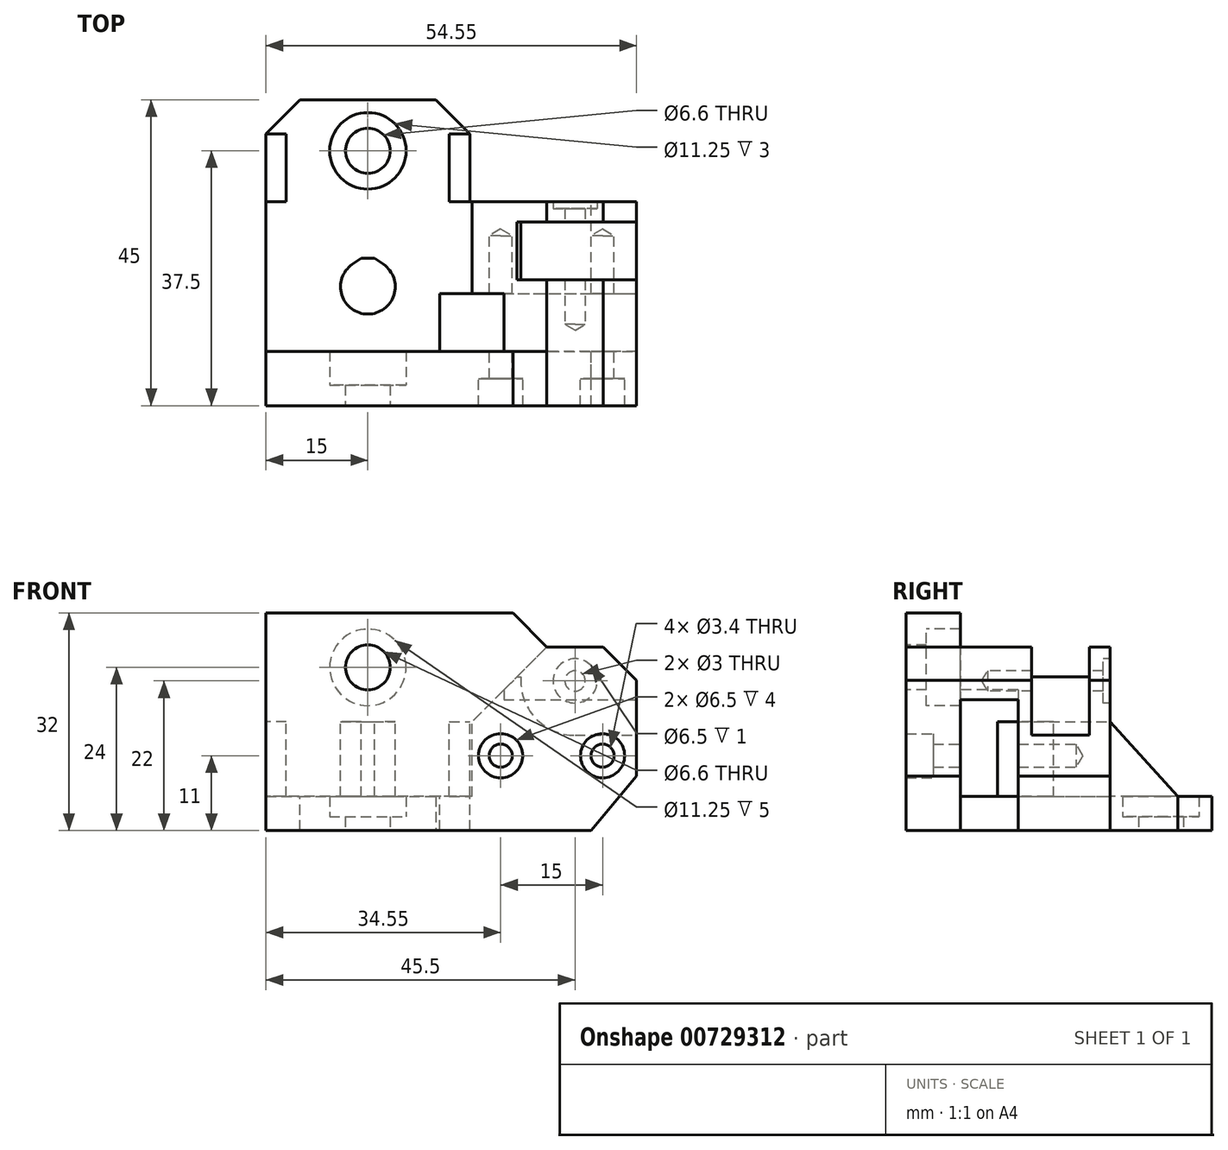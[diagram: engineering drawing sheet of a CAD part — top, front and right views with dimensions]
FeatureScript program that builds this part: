
annotation { "Feature Type Name" : "Feature", "Feature Type Description" : "" }
export const myFeature = defineFeature(function(context is Context, id is Id, definition is map)
    precondition{}
    {
        {
            var Q0;
            Q0=qCreatedBy(makeId("Front.planeOp"),FACE);
            var sketch = newSketch(context, id + "F0", { "sketchPlane" : qUnion([Q0])});
            skLineSegment(sketch, "E0", {"start": v(19.55, 11) * mm, "end": v(34.55, 11) * mm, "construction": true});
            skLineSegment(sketch, "E1", {"start": v(34.55, 11) * mm, "end": v(30.5, 22) * mm, "construction": true});
            skLineSegment(sketch, "E2", {"start": v(30.5, 22) * mm, "end": v(19.55, 11) * mm, "construction": true});
            skPoint(sketch, "E3", {"position": v(30.5, 22) * mm});
            skPoint(sketch, "E4", {"position": v(34.55, 11) * mm});
            skPoint(sketch, "E5", {"position": v(19.55, 11) * mm});
            skCircle(sketch, "E6", {"center": v(30.5, 22) * mm, "radius": 1.5 * mm, "construction": true});
            skCircle(sketch, "E7", {"center": v(34.55, 11) * mm, "radius": 1.5 * mm, "construction": true});
            skCircle(sketch, "E8", {"center": v(19.55, 11) * mm, "radius": 1.5 * mm, "construction": true});
            skPoint(sketch, "E9", {"position": v(0, 0) * mm});
            skCircle(sketch, "E10", {"center": v(30.5, 22) * mm, "radius": 6.5 * mm, "construction": true});
            skCircle(sketch, "E11", {"center": v(34.55, 11) * mm, "radius": 6.5 * mm, "construction": true});
            skCircle(sketch, "E12", {"center": v(19.55, 11) * mm, "radius": 6.5 * mm, "construction": true});
            skPoint(sketch, "E13", {"position": v(34.55, 12.5) * mm});
            skPoint(sketch, "E14", {"position": v(30.5, 15.5) * mm});
            skSolve(sketch);
        }
        {
            var Q0;
            Q0=qCreatedBy(makeId("Front.planeOp"),FACE);
            cPlane(context, id + "F1", {"entities" : qUnion([Q0]), "cplaneType" : CPlaneType.OFFSET, "offset" : 12.5 * mm, "oppositeDirection" : true, "width" : 150 * mm, "height" : 150 * mm});
        }
        {
            var Q0;
            Q0=qCreatedBy(id+"F1.planeOp",FACE);
            cPlane(context, id + "F2", {"entities" : qUnion([Q0]), "cplaneType" : CPlaneType.OFFSET, "offset" : 30 * mm, "width" : 150 * mm, "height" : 150 * mm});
        }
        {
            var Q0;
            Q0=qCreatedBy(id+"F1.planeOp",FACE);
            var sketch = newSketch(context, id + "F3", { "sketchPlane" : qUnion([Q0])});
            skLineSegment(sketch, "E15.0", {"start": v(39.55, 8) * mm, "end": v(32.84, 0) * mm});
            skLineSegment(sketch, "E16.0", {"start": v(32.84, 0) * mm, "end": v(-15, 0) * mm});
            skPoint(sketch, "E17.0", {"position": v(30.5, 22) * mm});
            skLineSegment(sketch, "E18", {"start": v(39.55, 8) * mm, "end": v(39.55, 22.1) * mm});
            skLineSegment(sketch, "E19", {"start": v(39.55, 22.1) * mm, "end": v(34.65, 27) * mm});
            skLineSegment(sketch, "E20", {"start": v(34.65, 27) * mm, "end": v(26.35, 27) * mm});
            skLineSegment(sketch, "E21", {"start": v(26.35, 27) * mm, "end": v(15.35, 16) * mm});
            skLineSegment(sketch, "E22", {"start": v(15.35, 16) * mm, "end": v(-15, 16) * mm});
            skLineSegment(sketch, "E23", {"start": v(-15, 16) * mm, "end": v(-15, 0) * mm});
            skSolve(sketch);
        }
        {
            var Q0;
            Q0=makeQuery(id+"F3.imprint","IMPRINT",FACE,{"disambiguationData":[TD([[makeQuery(id+"F3.imprint","IMPRINT",EDGE,{"derivedFrom":sQuery(id+"F3.wireOp",EDGE,"E15.0")}),-1.0]])]});
            var Q1;
            Q1=qCreatedBy(makeId("Front.planeOp"),FACE);
            extrude(context, id + "F4", {"entities" : qUnion([Q0]), "endBound" : BoundingType.UP_TO_SURFACE, "depth" : 25 * mm, "endBoundEntityFace" : qUnion([Q1]), "offsetDistance" : 25 * mm});
        }
        {
            var Q0;
            Q0=qCreatedBy(makeId("Front.planeOp"),FACE);
            cPlane(context, id + "F5", {"entities" : qUnion([Q0]), "cplaneType" : CPlaneType.OFFSET, "offset" : 1 * mm, "oppositeDirection" : true, "width" : 150 * mm, "height" : 150 * mm});
        }
        {
            var Q0;
            Q0=qCreatedBy(id+"F5.planeOp",FACE);
            var sketch = newSketch(context, id + "F6", { "sketchPlane" : qUnion([Q0])});
            skArc(sketch, "E24", {"start": v(25.84, 28.5) * mm, "mid": v(22.88, 19.55) * mm, "end": v(30.5, 14) * mm});
            skLineSegment(sketch, "E25", {"start": v(30.5, 14) * mm, "end": v(39.55, 14) * mm});
            skLineSegment(sketch, "E26", {"start": v(39.55, 14) * mm, "end": v(39.55, 28.5) * mm});
            skLineSegment(sketch, "E27", {"start": v(39.55, 28.5) * mm, "end": v(25.84, 28.5) * mm});
            skSolve(sketch);
        }
        {
            var Q0;
            Q0=makeQuery(id+"F6.imprint","IMPRINT",FACE,{"disambiguationData":[TD([[makeQuery(id+"F6.imprint","IMPRINT",EDGE,{"derivedFrom":sQuery(id+"F6.wireOp",EDGE,"E24")}),1.0]])]});
            extrude(context, id + "F7", {"entities" : qUnion([Q0]), "operationType" : NewBodyOperationType.REMOVE, "oppositeDirection" : true, "depth" : 8.5 * mm, "offsetDistance" : 25 * mm});
        }
        {
            var Q0;
            Q0=makeQuery(id+"F7.boolean.opBoolean","INTERSECT",EDGE,{"derivedFrom":[makeQuery(id+"F4.opExtrude","SWEPT_FACE",FACE,{"disambiguationData":[OSD([sQuery(id+"F3.wireOp",EDGE,"E21")])]}),makeQuery(id+"F7.opExtrude","SWEPT_FACE",FACE,{"disambiguationData":[OSD([sQuery(id+"F6.wireOp",EDGE,"E24")])]})]});
            chamfer(context, id + "F8", {"entities" : qUnion([Q0]), "chamferType" : ChamferType.OFFSET_ANGLE, "width" : 1 * mm, "oppositeDirection" : false, "angle" : 45 * degree, "tangentPropagation" : true});
        }
        {
            var Q0;
            Q0=qCreatedBy(id+"F2.planeOp",FACE);
            var sketch = newSketch(context, id + "F9", { "sketchPlane" : qUnion([Q0])});
            skLineSegment(sketch, "E28.0", {"start": v(-15, 16) * mm, "end": v(-15, 0) * mm});
            skLineSegment(sketch, "E29.0", {"start": v(32.84, 0) * mm, "end": v(-15, 0) * mm});
            skLineSegment(sketch, "E30.0", {"start": v(39.55, 8) * mm, "end": v(32.84, 0) * mm});
            skLineSegment(sketch, "E31", {"start": v(-15, 16) * mm, "end": v(39.55, 16) * mm});
            skLineSegment(sketch, "E32", {"start": v(39.55, 16) * mm, "end": v(39.55, 8) * mm});
            skPoint(sketch, "E33.0", {"position": v(19.55, 11) * mm});
            skPoint(sketch, "E34.0", {"position": v(34.55, 11) * mm});
            skSolve(sketch);
        }
        {
            var Q0;
            Q0=makeQuery(id+"F9.imprint","IMPRINT",FACE,{"disambiguationData":[TD([[makeQuery(id+"F9.imprint","IMPRINT",EDGE,{"derivedFrom":sQuery(id+"F9.wireOp",EDGE,"E28.0")}),1.0]])]});
            var Q1;
            Q1=qCreatedBy(makeId("Front.planeOp"),FACE);
            extrude(context, id + "F10", {"entities" : qUnion([Q0]), "operationType" : NewBodyOperationType.ADD, "endBound" : BoundingType.UP_TO_SURFACE, "oppositeDirection" : true, "depth" : 25 * mm, "endBoundEntityFace" : qUnion([Q1]), "offsetDistance" : 25 * mm});
        }
        {
            var Q0;
            Q0=makeQuery(id+"F4.opExtrude","CAP_FACE",FACE,{"disambiguationData":[OSD([sQuery(id+"F3.wireOp",EDGE,"E15.0"),sQuery(id+"F3.wireOp",EDGE,"E16.0"),sQuery(id+"F3.wireOp",EDGE,"E18"),sQuery(id+"F3.wireOp",EDGE,"E19"),sQuery(id+"F3.wireOp",EDGE,"E20"),sQuery(id+"F3.wireOp",EDGE,"E21"),sQuery(id+"F3.wireOp",EDGE,"E22"),sQuery(id+"F3.wireOp",EDGE,"E23")])],"isStart":false});
            extrude(context, id + "F11", {"entities" : qUnion([Q0]), "operationType" : NewBodyOperationType.ADD, "depth" : 1 * mm, "offsetDistance" : 25 * mm});
        }
        {
            var Q0;
            Q0=makeQuery(id+"F10.boolean.opBoolean","MERGE",FACE,{"derivedFrom":[makeQuery(id+"F4.opExtrude","SWEPT_FACE",FACE,{"disambiguationData":[OSD([sQuery(id+"F3.wireOp",EDGE,"E22")])]}),makeQuery(id+"F10.opExtrude","SWEPT_FACE",FACE,{"disambiguationData":[OSD([sQuery(id+"F9.wireOp",EDGE,"E31")])]})]});
            var sketch = newSketch(context, id + "F12", { "sketchPlane" : qUnion([Q0])});
            skLineSegment(sketch, "E35.bottom", {"start": v(39.55, -1) * mm, "end": v(10.55, -1) * mm});
            skLineSegment(sketch, "E35.top", {"start": v(39.55, -9.5) * mm, "end": v(10.55, -9.5) * mm});
            skLineSegment(sketch, "E35.left", {"start": v(39.55, -1) * mm, "end": v(39.55, -9.5) * mm});
            skLineSegment(sketch, "E35.right", {"start": v(10.55, -1) * mm, "end": v(10.55, -9.5) * mm});
            skSolve(sketch);
        }
        {
            var Q0;
            Q0=makeQuery(id+"F12.imprint","IMPRINT",FACE,{"disambiguationData":[TD([[makeQuery(id+"F12.imprint","IMPRINT",EDGE,{"derivedFrom":sQuery(id+"F12.wireOp",EDGE,"E35.top")}),-1.0]])]});
            extrude(context, id + "F13", {"entities" : qUnion([Q0]), "operationType" : NewBodyOperationType.REMOVE, "oppositeDirection" : true, "depth" : 25 * mm, "offsetDistance" : 25 * mm});
        }
        {
            var Q0;
            Q0=qCreatedBy(id+"F2.planeOp",FACE);
            var sketch = newSketch(context, id + "F14", { "sketchPlane" : qUnion([Q0])});
            skLineSegment(sketch, "E36.0", {"start": v(32.84, 0) * mm, "end": v(-15, 0) * mm});
            skLineSegment(sketch, "E37.0", {"start": v(39.55, 8) * mm, "end": v(32.84, 0) * mm});
            skLineSegment(sketch, "E38.0", {"start": v(39.55, 16) * mm, "end": v(39.55, 8) * mm});
            skLineSegment(sketch, "E39.0", {"start": v(39.55, 8) * mm, "end": v(39.55, 22.1) * mm});
            skLineSegment(sketch, "E40.0", {"start": v(39.55, 22.1) * mm, "end": v(34.65, 27) * mm});
            skLineSegment(sketch, "E41.0", {"start": v(34.65, 27) * mm, "end": v(26.35, 27) * mm});
            skLineSegment(sketch, "E42", {"start": v(-15, 0) * mm, "end": v(-15, 32) * mm});
            skLineSegment(sketch, "E43", {"start": v(-15, 32) * mm, "end": v(21.35, 32) * mm});
            skLineSegment(sketch, "E44", {"start": v(21.35, 32) * mm, "end": v(26.35, 27) * mm});
            skSolve(sketch);
        }
        {
            var Q0;
            Q0=makeQuery(id+"F14.imprint","IMPRINT",FACE,{"disambiguationData":[TD([[makeQuery(id+"F14.imprint","IMPRINT",EDGE,{"derivedFrom":sQuery(id+"F14.wireOp",EDGE,"E36.0")}),-1.0]])]});
            extrude(context, id + "F15", {"entities" : qUnion([Q0]), "operationType" : NewBodyOperationType.ADD, "oppositeDirection" : true, "depth" : 8 * mm, "offsetDistance" : 25 * mm});
        }
        {
            var Q0;
            Q0=makeQuery(id+"F13.boolean.opBoolean","MERGE",FACE,{"derivedFrom":[makeQuery(id+"F11.opExtrude","CAP_FACE",FACE,{"disambiguationData":[OSD([sQuery(id+"F3.wireOp",EDGE,"E15.0"),sQuery(id+"F3.wireOp",EDGE,"E16.0"),sQuery(id+"F3.wireOp",EDGE,"E18"),sQuery(id+"F3.wireOp",EDGE,"E19"),sQuery(id+"F3.wireOp",EDGE,"E20"),sQuery(id+"F3.wireOp",EDGE,"E21"),sQuery(id+"F3.wireOp",EDGE,"E22"),sQuery(id+"F3.wireOp",EDGE,"E23")])],"isStart":false})],"fromTools":[makeQuery(id+"F13.opExtrude","SWEPT_FACE",FACE,{"disambiguationData":[OSD([sQuery(id+"F12.wireOp",EDGE,"E35.bottom")])]})]});
            var sketch = newSketch(context, id + "F16", { "sketchPlane" : qUnion([Q0])});
            skLineSegment(sketch, "E45", {"start": v(39.55, 22.1) * mm, "end": v(34.65, 27) * mm});
            skLineSegment(sketch, "E46", {"start": v(34.65, 27) * mm, "end": v(26.35, 27) * mm});
            skLineSegment(sketch, "E47", {"start": v(26.35, 27) * mm, "end": v(18.6, 19.25) * mm});
            skLineSegment(sketch, "E48", {"start": v(18.6, 19.25) * mm, "end": v(39.55, 19.25) * mm});
            skLineSegment(sketch, "E49", {"start": v(39.55, 19.25) * mm, "end": v(39.55, 22.1) * mm});
            skSolve(sketch);
        }
        {
            var Q0;
            Q0 = qSketchRegion(id + "F16", true);
            var Q1;
            Q1=makeQuery(id+"F15.boolean.opBoolean","MERGE",FACE,{"derivedFrom":[makeQuery(id+"F13.boolean.opBoolean","COPY",FACE,{"derivedFrom":makeQuery(id+"F13.opExtrude","SWEPT_FACE",FACE,{"disambiguationData":[OSD([sQuery(id+"F12.wireOp",EDGE,"E35.top")])]})}),makeQuery(id+"F15.opExtrude","CAP_FACE",FACE,{"disambiguationData":[OSD([sQuery(id+"F14.wireOp",EDGE,"E36.0"),sQuery(id+"F14.wireOp",EDGE,"E37.0"),sQuery(id+"F14.wireOp",EDGE,"E38.0"),sQuery(id+"F14.wireOp",EDGE,"E39.0"),sQuery(id+"F14.wireOp",EDGE,"E40.0"),sQuery(id+"F14.wireOp",EDGE,"E41.0"),sQuery(id+"F14.wireOp",EDGE,"E42"),sQuery(id+"F14.wireOp",EDGE,"E43"),sQuery(id+"F14.wireOp",EDGE,"E44")])],"isStart":false})]});
            extrude(context, id + "F17", {"entities" : qUnion([Q0]), "operationType" : NewBodyOperationType.ADD, "endBound" : BoundingType.UP_TO_SURFACE, "depth" : 25 * mm, "endBoundEntityFace" : qUnion([Q1]), "offsetDistance" : 25 * mm});
        }
        {
            var Q0;
            Q0=makeQuery(id+"F17.opExtrude","SWEPT_EDGE",EDGE,{"disambiguationData":[OSD([sQuery(id+"F3.wireOp",EDGE,"E21"),sQuery(id+"F16.wireOp",EDGE,"E47"),sQuery(id+"F16.wireOp",EDGE,"E48")])]});
            chamfer(context, id + "F18", {"entities" : qUnion([Q0]), "chamferType" : ChamferType.OFFSET_ANGLE, "width" : 2 * mm, "oppositeDirection" : true, "angle" : 45 * degree, "tangentPropagation" : true});
        }
        {
            var Q0;
            Q0=sQuery(id+"F3.wireOp",VERTEX,"E17.0");
            var Q1;
            Q1=makeQuery(id+"F4.opExtrude","SWEPT_BODY",BODY,{"disambiguationData":[OSD([sQuery(id+"F3.wireOp",EDGE,"E15.0"),sQuery(id+"F3.wireOp",EDGE,"E16.0"),sQuery(id+"F3.wireOp",EDGE,"E18"),sQuery(id+"F3.wireOp",EDGE,"E19"),sQuery(id+"F3.wireOp",EDGE,"E20"),sQuery(id+"F3.wireOp",EDGE,"E21"),sQuery(id+"F3.wireOp",EDGE,"E22"),sQuery(id+"F3.wireOp",EDGE,"E23")])]});
            hole(context, id + "F19", {"style" : HoleStyle.C_BORE, "endStyle" : HoleEndStyle.BLIND, "oppositeDirection" : true, "holeDiameter" : 3 * mm, "cBoreDiameter" : 6.5 * mm, "cBoreDepth" : 1 * mm, "majorDiameter" : 5 * mm, "holeDepth" : 18 * mm, "isTappedThrough" : true, "tappedDepth" : 12 * mm, "tapClearance" : 3, "locations" : qUnion([Q0]), "scope" : qUnion([Q1])});
        }
        {
            var Q0;
            Q0=makeQuery(id+"F15.boolean.opBoolean","MERGE",FACE,{"derivedFrom":[makeQuery(id+"F10.opExtrude","CAP_FACE",FACE,{"disambiguationData":[OSD([sQuery(id+"F9.wireOp",EDGE,"E28.0"),sQuery(id+"F9.wireOp",EDGE,"E29.0"),sQuery(id+"F9.wireOp",EDGE,"E30.0"),sQuery(id+"F9.wireOp",EDGE,"E31"),sQuery(id+"F9.wireOp",EDGE,"E32")])],"isStart":true}),makeQuery(id+"F15.opExtrude","CAP_FACE",FACE,{"disambiguationData":[OSD([sQuery(id+"F14.wireOp",EDGE,"E36.0"),sQuery(id+"F14.wireOp",EDGE,"E37.0"),sQuery(id+"F14.wireOp",EDGE,"E38.0"),sQuery(id+"F14.wireOp",EDGE,"E39.0"),sQuery(id+"F14.wireOp",EDGE,"E40.0"),sQuery(id+"F14.wireOp",EDGE,"E41.0"),sQuery(id+"F14.wireOp",EDGE,"E42"),sQuery(id+"F14.wireOp",EDGE,"E43"),sQuery(id+"F14.wireOp",EDGE,"E44")])],"isStart":true})]});
            var sketch = newSketch(context, id + "F20", { "sketchPlane" : qUnion([Q0])});
            skPoint(sketch, "E50", {"position": v(0, 0) * mm});
            skSolve(sketch);
        }
        {
            var Q0;
            Q0=makeQuery(id+"F15.boolean.opBoolean","MERGE",FACE,{"derivedFrom":[makeQuery(id+"F13.boolean.opBoolean","COPY",FACE,{"derivedFrom":makeQuery(id+"F13.opExtrude","SWEPT_FACE",FACE,{"disambiguationData":[OSD([sQuery(id+"F12.wireOp",EDGE,"E35.top")])]})}),makeQuery(id+"F15.opExtrude","CAP_FACE",FACE,{"disambiguationData":[OSD([sQuery(id+"F14.wireOp",EDGE,"E36.0"),sQuery(id+"F14.wireOp",EDGE,"E37.0"),sQuery(id+"F14.wireOp",EDGE,"E38.0"),sQuery(id+"F14.wireOp",EDGE,"E39.0"),sQuery(id+"F14.wireOp",EDGE,"E40.0"),sQuery(id+"F14.wireOp",EDGE,"E41.0"),sQuery(id+"F14.wireOp",EDGE,"E42"),sQuery(id+"F14.wireOp",EDGE,"E43"),sQuery(id+"F14.wireOp",EDGE,"E44")])],"isStart":false})]});
            var sketch = newSketch(context, id + "F21", { "sketchPlane" : qUnion([Q0])});
            skLineSegment(sketch, "E51", {"start": v(0, 16) * mm, "end": v(0, 32) * mm, "construction": true});
            skPoint(sketch, "E52", {"position": v(0, 24) * mm});
            skSolve(sketch);
        }
        {
            var Q0;
            Q0=sQuery(id+"F21.wireOp",VERTEX,"E52");
            var Q1;
            Q1=makeQuery(id+"F4.opExtrude","SWEPT_BODY",BODY,{"disambiguationData":[OSD([sQuery(id+"F3.wireOp",EDGE,"E15.0"),sQuery(id+"F3.wireOp",EDGE,"E16.0"),sQuery(id+"F3.wireOp",EDGE,"E18"),sQuery(id+"F3.wireOp",EDGE,"E19"),sQuery(id+"F3.wireOp",EDGE,"E20"),sQuery(id+"F3.wireOp",EDGE,"E21"),sQuery(id+"F3.wireOp",EDGE,"E22"),sQuery(id+"F3.wireOp",EDGE,"E23")])]});
            hole(context, id + "F22", {"style" : HoleStyle.C_BORE, "endStyle" : HoleEndStyle.BLIND, "holeDiameter" : 6.6 * mm, "cBoreDiameter" : 11.25 * mm, "cBoreDepth" : 5 * mm, "majorDiameter" : 5 * mm, "holeDepth" : 18 * mm, "isTappedThrough" : true, "tappedDepth" : 12 * mm, "tapClearance" : 3, "locations" : qUnion([Q0]), "scope" : qUnion([Q1])});
        }
        {
            var Q0;
            Q0=makeQuery(id+"F3.imprint","IMPRINT",FACE,{"disambiguationData":[TD([[makeQuery(id+"F3.imprint","IMPRINT",EDGE,{"derivedFrom":sQuery(id+"F3.wireOp",EDGE,"E15.0")}),-1.0]])]});
            var sketch = newSketch(context, id + "F23", { "sketchPlane" : qUnion([Q0])});
            skLineSegment(sketch, "E53.bottom", {"start": v(-15, 0) * mm, "end": v(15, 0) * mm});
            skLineSegment(sketch, "E53.top", {"start": v(-15, 5) * mm, "end": v(15, 5) * mm});
            skLineSegment(sketch, "E53.left", {"start": v(-15, 0) * mm, "end": v(-15, 5) * mm});
            skLineSegment(sketch, "E53.right", {"start": v(15, 0) * mm, "end": v(15, 5) * mm});
            skSolve(sketch);
        }
        {
            var Q0;
            Q0=makeQuery(id+"F23.imprint","IMPRINT",FACE,{"disambiguationData":[TD([[makeQuery(id+"F23.imprint","IMPRINT",EDGE,{"derivedFrom":sQuery(id+"F23.wireOp",EDGE,"E53.bottom")}),-1.0]])]});
            extrude(context, id + "F24", {"entities" : qUnion([Q0]), "operationType" : NewBodyOperationType.ADD, "oppositeDirection" : true, "depth" : 15 * mm, "offsetDistance" : 25 * mm});
        }
        {
            var Q0;
            Q0=makeQuery(id+"F24.opExtrude","SWEPT_FACE",FACE,{"disambiguationData":[OSD([sQuery(id+"F23.wireOp",EDGE,"E53.top")])]});
            var sketch = newSketch(context, id + "F25", { "sketchPlane" : qUnion([Q0])});
            skLineSegment(sketch, "E54", {"start": v(0, 27.5) * mm, "end": v(0, 12.5) * mm, "construction": true});
            skPoint(sketch, "E55", {"position": v(0, 20) * mm});
            skSolve(sketch);
        }
        {
            var Q0;
            Q0=sQuery(id+"F25.wireOp",VERTEX,"E55");
            var Q1;
            Q1=makeQuery(id+"F4.opExtrude","SWEPT_BODY",BODY,{"disambiguationData":[OSD([sQuery(id+"F3.wireOp",EDGE,"E15.0"),sQuery(id+"F3.wireOp",EDGE,"E16.0"),sQuery(id+"F3.wireOp",EDGE,"E18"),sQuery(id+"F3.wireOp",EDGE,"E19"),sQuery(id+"F3.wireOp",EDGE,"E20"),sQuery(id+"F3.wireOp",EDGE,"E21"),sQuery(id+"F3.wireOp",EDGE,"E22"),sQuery(id+"F3.wireOp",EDGE,"E23")])]});
            hole(context, id + "F26", {"style" : HoleStyle.C_BORE, "endStyle" : HoleEndStyle.BLIND, "holeDiameter" : 6.6 * mm, "cBoreDiameter" : 11.25 * mm, "cBoreDepth" : 3 * mm, "majorDiameter" : 5 * mm, "holeDepth" : 18 * mm, "isTappedThrough" : true, "tappedDepth" : 12 * mm, "tapClearance" : 3, "locations" : qUnion([Q0]), "scope" : qUnion([Q1])});
        }
        {
            var Q0;
            Q0=makeQuery(id+"F24.opExtrude","CAP_EDGE",EDGE,{"disambiguationData":[OSD([sQuery(id+"F23.wireOp",EDGE,"E53.right")])],"isStart":false});
            var Q1;
            Q1=makeQuery(id+"F24.opExtrude","CAP_EDGE",EDGE,{"disambiguationData":[OSD([sQuery(id+"F23.wireOp",EDGE,"E53.left")])],"isStart":false});
            chamfer(context, id + "F27", {"entities" : qUnion([Q0, Q1]), "width" : 5 * mm, "tangentPropagation" : true});
        }
        {
            var Q0;
            Q0=makeQuery(id+"F24.boolean.opBoolean","MERGE",FACE,{"derivedFrom":[makeQuery(id+"F15.boolean.opBoolean","MERGE",FACE,{"derivedFrom":[makeQuery(id+"F10.boolean.opBoolean","MERGE",FACE,{"derivedFrom":[makeQuery(id+"F4.opExtrude","SWEPT_FACE",FACE,{"disambiguationData":[OSD([sQuery(id+"F3.wireOp",EDGE,"E23")])]}),makeQuery(id+"F10.opExtrude","SWEPT_FACE",FACE,{"disambiguationData":[OSD([sQuery(id+"F9.wireOp",EDGE,"E28.0")])]})]}),makeQuery(id+"F15.opExtrude","SWEPT_FACE",FACE,{"disambiguationData":[OSD([sQuery(id+"F14.wireOp",EDGE,"E42")])]})]}),makeQuery(id+"F24.opExtrude","SWEPT_FACE",FACE,{"disambiguationData":[OSD([sQuery(id+"F23.wireOp",EDGE,"E53.left")])]})]});
            var sketch = newSketch(context, id + "F28", { "sketchPlane" : qUnion([Q0])});
            skLineSegment(sketch, "E56", {"start": v(-22.5, 5) * mm, "end": v(-12.5, 16) * mm});
            skLineSegment(sketch, "E57", {"start": v(-12.5, 16) * mm, "end": v(-12.5, 5) * mm});
            skLineSegment(sketch, "E58", {"start": v(-12.5, 5) * mm, "end": v(-22.5, 5) * mm});
            skSolve(sketch);
        }
        {
            var Q0;
            Q0=makeQuery(id+"F28.imprint","IMPRINT",FACE,{"disambiguationData":[TD([[makeQuery(id+"F28.imprint","IMPRINT",EDGE,{"derivedFrom":sQuery(id+"F28.wireOp",EDGE,"E56")}),-1.0]])]});
            extrude(context, id + "F29", {"entities" : qUnion([Q0]), "operationType" : NewBodyOperationType.ADD, "oppositeDirection" : true, "depth" : 3 * mm, "offsetDistance" : 25 * mm});
        }
        {
            var Q0;
            Q0=makeQuery(id+"F24.opExtrude","SWEPT_FACE",FACE,{"disambiguationData":[OSD([sQuery(id+"F23.wireOp",EDGE,"E53.right")])]});
            var sketch = newSketch(context, id + "F30", { "sketchPlane" : qUnion([Q0])});
            skLineSegment(sketch, "E59", {"start": v(22.5, 5) * mm, "end": v(12.5, 16) * mm});
            skLineSegment(sketch, "E60", {"start": v(12.5, 16) * mm, "end": v(12.5, 5) * mm});
            skLineSegment(sketch, "E61", {"start": v(12.5, 5) * mm, "end": v(22.5, 5) * mm});
            skSolve(sketch);
        }
        {
            var Q0;
            Q0=makeQuery(id+"F30.imprint","IMPRINT",FACE,{"disambiguationData":[TD([[makeQuery(id+"F30.imprint","IMPRINT",EDGE,{"derivedFrom":sQuery(id+"F30.wireOp",EDGE,"E59")}),1.0]])]});
            extrude(context, id + "F31", {"entities" : qUnion([Q0]), "operationType" : NewBodyOperationType.ADD, "oppositeDirection" : true, "depth" : 3 * mm, "offsetDistance" : 25 * mm});
        }
        {
            var Q0;
            Q0=makeQuery(id+"F10.boolean.opBoolean","MERGE",FACE,{"derivedFrom":[makeQuery(id+"F4.opExtrude","SWEPT_FACE",FACE,{"disambiguationData":[OSD([sQuery(id+"F3.wireOp",EDGE,"E22")])]}),makeQuery(id+"F10.opExtrude","SWEPT_FACE",FACE,{"disambiguationData":[OSD([sQuery(id+"F9.wireOp",EDGE,"E31")])]})]});
            var sketch = newSketch(context, id + "F32", { "sketchPlane" : qUnion([Q0])});
            skArc(sketch, "E62", {"start": v(2.33, 3.28) * mm, "mid": v(0, -4.03) * mm, "end": v(-2.33, 3.28) * mm});
            skCircle(sketch, "E63", {"center": v(0, 0) * mm, "radius": 4.03 * mm, "construction": true});
            skLineSegment(sketch, "E64", {"start": v(-1, 4.23) * mm, "end": v(1, 4.23) * mm});
            skPoint(sketch, "E65", {"position": v(0, 4.23) * mm});
            skLineSegment(sketch, "E66", {"start": v(-1, 4.23) * mm, "end": v(-2.33, 3.28) * mm});
            skLineSegment(sketch, "E67", {"start": v(1, 4.22) * mm, "end": v(2.33, 3.28) * mm});
            skSolve(sketch);
        }
        {
            var Q0;
            Q0=makeQuery(id+"F32.imprint","IMPRINT",FACE,{"disambiguationData":[TD([[makeQuery(id+"F32.imprint","IMPRINT",EDGE,{"derivedFrom":sQuery(id+"F32.wireOp",EDGE,"E62")}),-1.0]])]});
            extrude(context, id + "F33", {"entities" : qUnion([Q0]), "operationType" : NewBodyOperationType.REMOVE, "oppositeDirection" : true, "depth" : 11 * mm, "offsetDistance" : 25 * mm});
        }
        {
            var Q0;
            Q0=makeQuery(id+"F20.imprint","IMPRINT",FACE,{"disambiguationData":[TD([[makeQuery(id+"F20.imprint","IMPRINT",EDGE,{"derivedFrom":makeQuery(id+"F10.opExtrude","CAP_EDGE",EDGE,{"disambiguationData":[OSD([sQuery(id+"F9.wireOp",EDGE,"E29.0")])],"isStart":true})}),-1.0]])]});
            var sketch = newSketch(context, id + "F34", { "sketchPlane" : qUnion([Q0])});
            skPoint(sketch, "E68.0", {"position": v(19.55, 11) * mm});
            skPoint(sketch, "E69.0", {"position": v(34.55, 11) * mm});
            skSolve(sketch);
        }
        {
            var Q0;
            Q0=sQuery(id+"F34.wireOp",VERTEX,"E68.0");
            var Q1;
            Q1=sQuery(id+"F34.wireOp",VERTEX,"E69.0");
            var Q2;
            Q2=makeQuery(id+"F4.opExtrude","SWEPT_BODY",BODY,{"disambiguationData":[OSD([sQuery(id+"F3.wireOp",EDGE,"E15.0"),sQuery(id+"F3.wireOp",EDGE,"E16.0"),sQuery(id+"F3.wireOp",EDGE,"E18"),sQuery(id+"F3.wireOp",EDGE,"E19"),sQuery(id+"F3.wireOp",EDGE,"E20"),sQuery(id+"F3.wireOp",EDGE,"E21"),sQuery(id+"F3.wireOp",EDGE,"E22"),sQuery(id+"F3.wireOp",EDGE,"E23")])]});
            hole(context, id + "F35", {"style" : HoleStyle.C_BORE, "endStyle" : HoleEndStyle.BLIND, "holeDiameter" : 3.4 * mm, "cBoreDiameter" : 6.5 * mm, "cBoreDepth" : 4 * mm, "majorDiameter" : 5 * mm, "holeDepth" : 25 * mm, "isTappedThrough" : true, "tappedDepth" : 12 * mm, "tapClearance" : 3, "locations" : qUnion([Q0, Q1]), "scope" : qUnion([Q2])});
        }
    });
